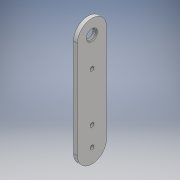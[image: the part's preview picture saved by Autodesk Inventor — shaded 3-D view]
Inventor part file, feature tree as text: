
AUTODESK INVENTOR PART (.ipt)
format: ipt  version: 2018 (Build 220112000, 112)  size: 120,320 bytes
history: native  units: mm
features: extrude x1, hole x1, sketch x1
ambient origin geometry x8: Origin, YZ Plane, XZ Plane, XY Plane, X Axis, Y Axis, Z Axis, Center Point
bodies: Body1 (feature_tree)
feature tree (3):
  extrude  "Extrusion6"  Depth=2.0mm
  hole  "Hole4"  [1 undecoded]
  sketch  "Sketch1"  dims[d6=15.0mm d18=100.0mm d40=10.0mm d50=0.0mm d51=0.0mm d52=20.0mm d53=30.0mm d54=4.0mm d55=4.0mm d56=0.0mm d57=10.0mm d58=10.0mm d59=11.6mm d60=6.0mm d61=4.0mm d62=2.0mm d63=90.0deg d64=0.8mm d65=20.594885mm]
note: 1 required parameter value undecoded (feature->parameter linkage not recoverable at this tier; creation-order binding heuristic only, values carry confidence <= 0.55)
